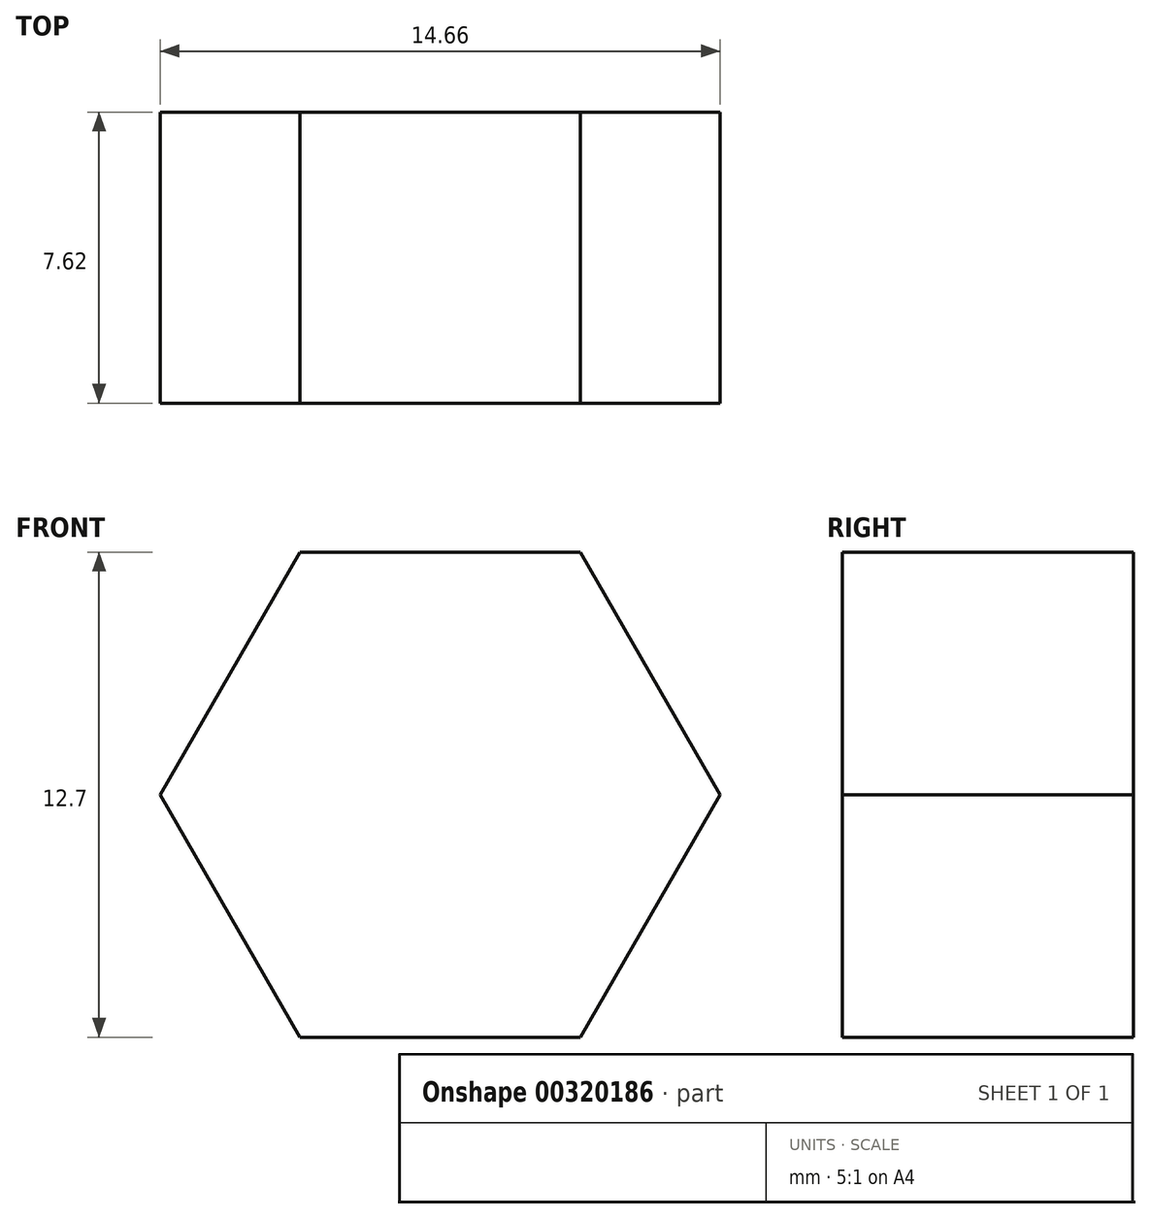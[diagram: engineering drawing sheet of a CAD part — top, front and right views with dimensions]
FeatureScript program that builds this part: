
annotation { "Feature Type Name" : "Feature", "Feature Type Description" : "" }
export const myFeature = defineFeature(function(context is Context, id is Id, definition is map)
    precondition{}
    {
        {
            var Q0;
            Q0=qCreatedBy(makeId("Front.planeOp"),FACE);
            var sketch = newSketch(context, id + "F0", { "sketchPlane" : qUnion([Q0])});
            skCircle(sketch, "E0.cCircle", {"center": v(0, 0) * mm, "radius": 6.35 * mm, "construction": true});
            skLineSegment(sketch, "E0.0", {"start": v(-3.67, 6.35) * mm, "end": v(3.67, 6.35) * mm});
            skLineSegment(sketch, "E0.1", {"start": v(3.67, 6.35) * mm, "end": v(7.33, 0) * mm});
            skLineSegment(sketch, "E0.2", {"start": v(7.33, 0) * mm, "end": v(3.67, -6.35) * mm});
            skLineSegment(sketch, "E0.3", {"start": v(3.67, -6.35) * mm, "end": v(-3.67, -6.35) * mm});
            skLineSegment(sketch, "E0.4", {"start": v(-3.67, -6.35) * mm, "end": v(-7.33, 0) * mm});
            skLineSegment(sketch, "E0.5", {"start": v(-7.33, 0) * mm, "end": v(-3.67, 6.35) * mm});
            skPoint(sketch, "E0.0.midPoint", {"position": v(0, 6.35) * mm});
            skSolve(sketch);
        }
        {
            var Q0;
            Q0 = qSketchRegion(id + "F0", true);
            extrude(context, id + "F1", {"entities" : qUnion([Q0]), "depth" : 7.62 * mm});
        }
    });
